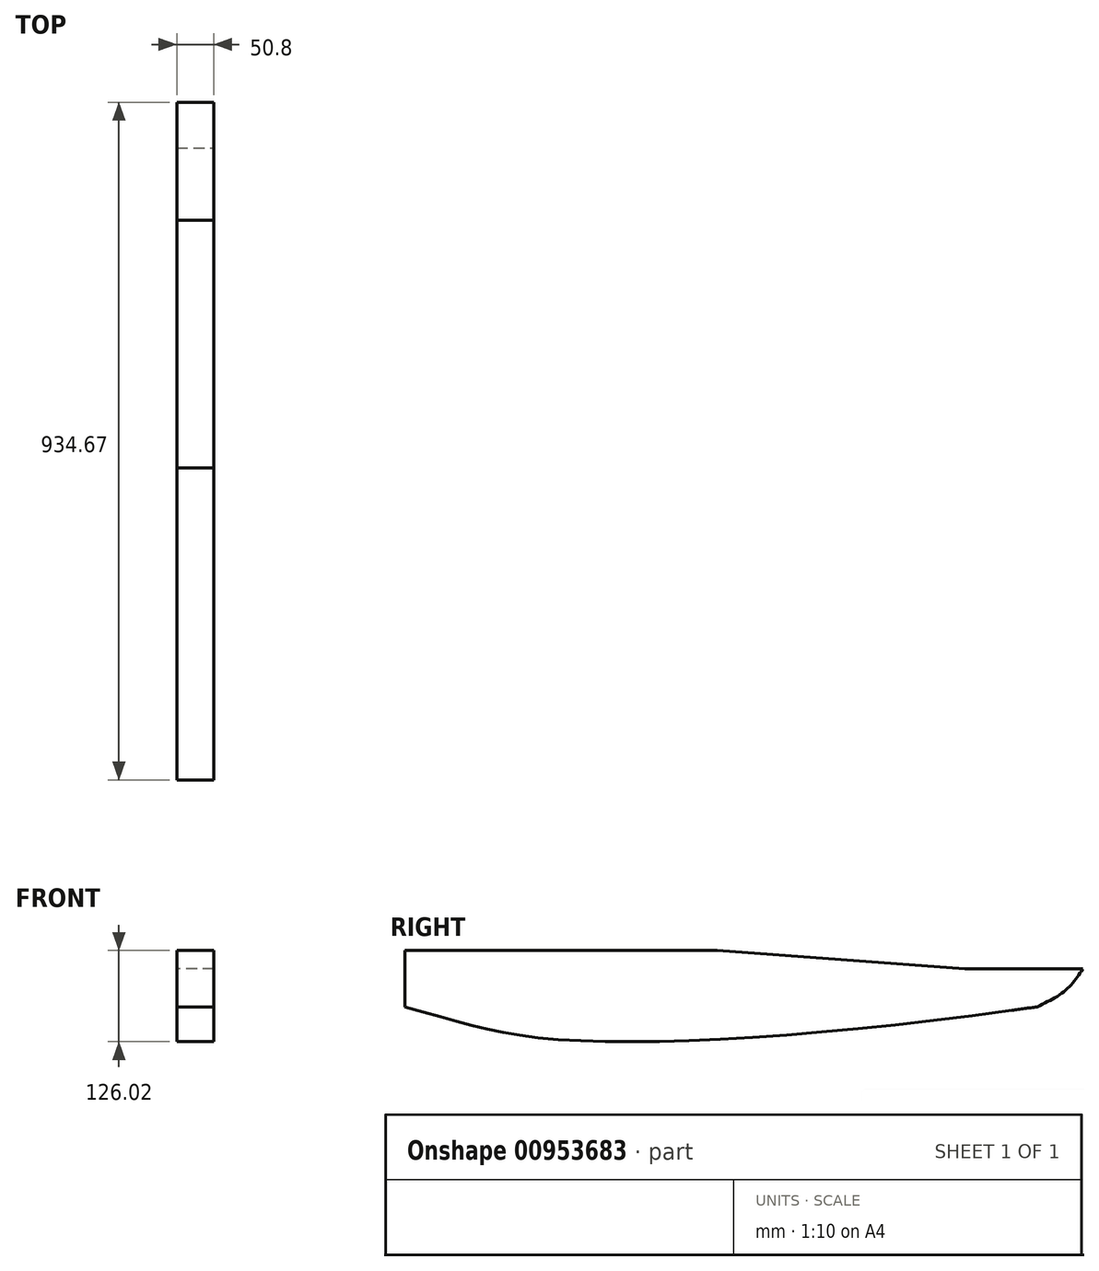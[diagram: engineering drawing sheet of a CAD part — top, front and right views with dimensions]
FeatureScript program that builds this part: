
annotation { "Feature Type Name" : "Feature", "Feature Type Description" : "" }
export const myFeature = defineFeature(function(context is Context, id is Id, definition is map)
    precondition{}
    {
        {
            var Q0;
            Q0=qCreatedBy(makeId("Right.planeOp"),FACE);
            var sketch = newSketch(context, id + "F0", { "sketchPlane" : qUnion([Q0])});
            skLineSegment(sketch, "E0", {"start": v(0, 77.9) * mm, "end": v(0, 0) * mm});
            skLineSegment(sketch, "E1", {"start": v(0, 77.9) * mm, "end": v(430.41, 77.9) * mm});
            skFitSpline(sketch, "E2", {"points": [v(0, 0) * mm, v(189.32, -43.12) * mm, v(871.6, 0) * mm], "startDerivative": vector(634.77, -169.82) * mm, "endDerivative": vector(1313.41, 189.91) * mm});
            skLineSegment(sketch, "E3", {"start": v(430.41, 77.9) * mm, "end": v(772.02, 52.2) * mm});
            skFitSpline(sketch, "E4", {"points": [v(871.6, 0) * mm, v(911.74, 23.58) * mm, v(934.67, 52.2) * mm], "startDerivative": vector(82.85, 40.24) * mm, "endDerivative": vector(42.48, 64.64) * mm});
            skLineSegment(sketch, "E5", {"start": v(836.96, -4.9) * mm, "end": v(871.6, 0) * mm});
            skLineSegment(sketch, "E6", {"start": v(934.67, 52.2) * mm, "end": v(772.02, 52.2) * mm});
            skSolve(sketch);
        }
        {
            var Q0;
            Q0 = qSketchRegion(id + "F0", true);
            extrude(context, id + "F1", {"entities" : qUnion([Q0]), "depth" : 50.8 * mm, "offsetDistance" : 25.4 * mm});
        }
    });
